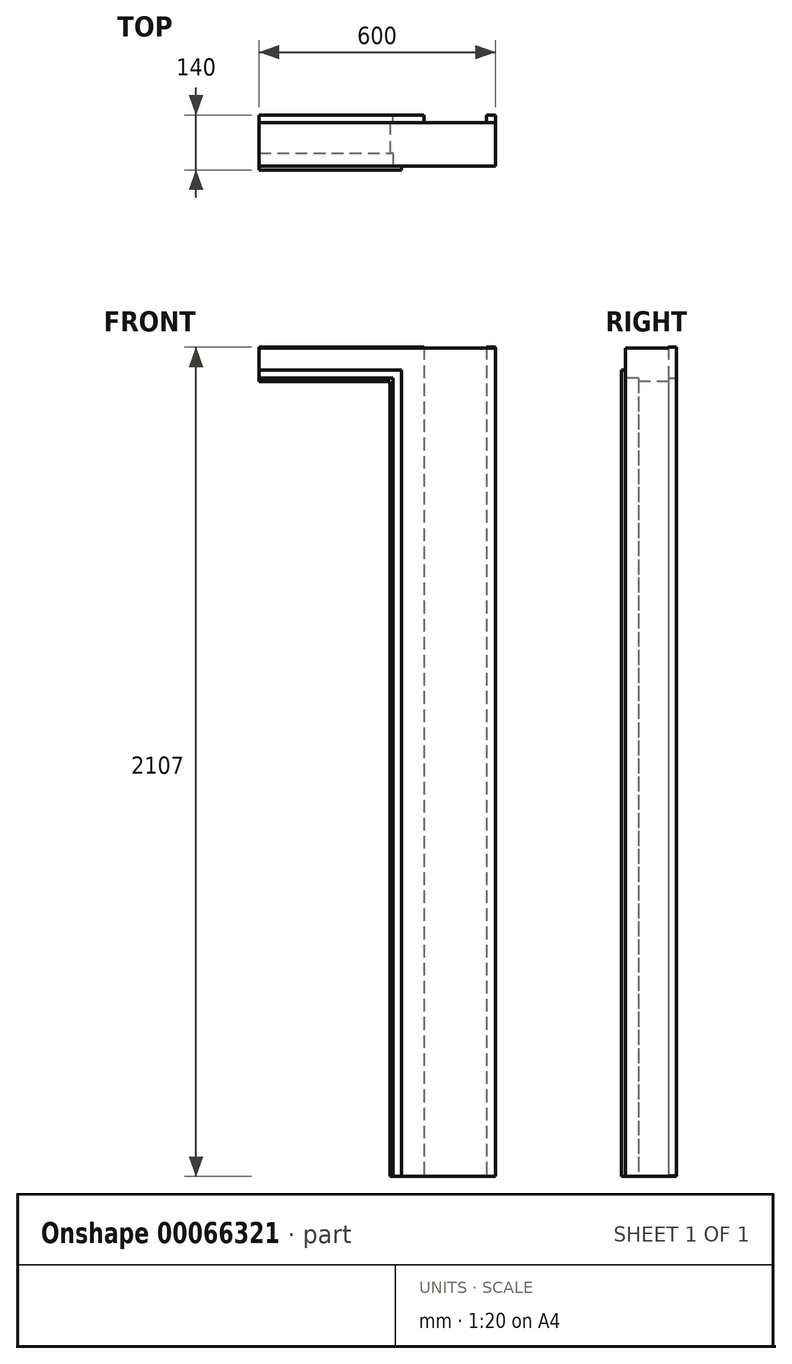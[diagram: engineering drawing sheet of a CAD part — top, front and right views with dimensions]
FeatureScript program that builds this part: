
annotation { "Feature Type Name" : "Feature", "Feature Type Description" : "" }
export const myFeature = defineFeature(function(context is Context, id is Id, definition is map)
    precondition{}
    {
        {
            var Q0;
            Q0=qCreatedBy(makeId("Front.planeOp"),FACE);
            var sketch = newSketch(context, id + "F0", { "sketchPlane" : qUnion([Q0])});
            skLineSegment(sketch, "E0.bottom", {"start": v(0, 0) * mm, "end": v(-600, 0) * mm});
            skLineSegment(sketch, "E0.top", {"start": v(0, -2105) * mm, "end": v(-260, -2105) * mm});
            skLineSegment(sketch, "E0.left", {"start": v(0, 0) * mm, "end": v(0, -2105) * mm});
            skLineSegment(sketch, "E0.right", {"start": v(-600, 0) * mm, "end": v(-600, -77) * mm});
            skLineSegment(sketch, "E1.top", {"start": v(-600, -77) * mm, "end": v(-260, -77) * mm});
            skLineSegment(sketch, "E1.right", {"start": v(-260, -2105) * mm, "end": v(-260, -77) * mm});
            skSolve(sketch);
        }
        {
            var Q0;
            Q0 = qSketchRegion(id + "F0", true);
            extrude(context, id + "F1", {"entities" : qUnion([Q0]), "oppositeDirection" : true, "depth" : (140 - 10 - 20) * mm});
        }
        {
            var Q0;
            Q0=makeQuery(id+"F1.opExtrude","CAP_FACE",FACE,{"disambiguationData":[OSD([sQuery(id+"F0.wireOp",EDGE,"E0.bottom"),sQuery(id+"F0.wireOp",EDGE,"E0.top"),sQuery(id+"F0.wireOp",EDGE,"E0.left"),sQuery(id+"F0.wireOp",EDGE,"E0.right"),sQuery(id+"F0.wireOp",EDGE,"E1.top"),sQuery(id+"F0.wireOp",EDGE,"E1.right")])],"isStart":true});
            var sketch = newSketch(context, id + "F2", { "sketchPlane" : qUnion([Q0])});
            skLineSegment(sketch, "E2", {"start": v(-600, -56) * mm, "end": v(-239, -56) * mm});
            skLineSegment(sketch, "E3", {"start": v(-239, -56) * mm, "end": v(-239, -2105) * mm});
            skLineSegment(sketch, "E4", {"start": v(-260, -77) * mm, "end": v(-239, -56) * mm, "construction": true});
            skSolve(sketch);
        }
        {
            var Q0;
            {var subQ3=sQuery(id+"F2.wireOp",EDGE,"E2");Q0=makeQuery(id+"F2.imprint","IMPRINT",FACE,{"disambiguationData":[TD([[makeQuery(id+"F2.imprint","IMPRINT",EDGE,{"derivedFrom":subQ3}),-1.0]])]});}
            extrude(context, id + "F3", {"entities" : qUnion([Q0]), "operationType" : NewBodyOperationType.ADD, "depth" : 10 * mm});
        }
        {
            var Q0;
            {var subQ0=sQuery(id+"F0.wireOp",EDGE,"E0.right");Q0=makeQuery(id+"F3.boolean.opBoolean","MERGE",FACE,{"derivedFrom":[makeQuery(id+"F1.opExtrude","SWEPT_FACE",FACE,{"disambiguationData":[OSD([subQ0])]}),makeQuery(id+"F3.opExtrude","SWEPT_FACE",FACE,{"disambiguationData":[OSD([subQ0])]})]});}
            var sketch = newSketch(context, id + "F4", { "sketchPlane" : qUnion([Q0])});
            skLineSegment(sketch, "E5.bottom", {"start": v(-110, -77) * mm, "end": v(-33, -77) * mm});
            skLineSegment(sketch, "E5.top", {"start": v(-110, -85) * mm, "end": v(-33, -85) * mm});
            skLineSegment(sketch, "E5.left", {"start": v(-110, -77) * mm, "end": v(-110, -85) * mm});
            skLineSegment(sketch, "E5.right", {"start": v(-33, -77) * mm, "end": v(-33, -85) * mm});
            skLineSegment(sketch, "E6.bottom", {"start": v(-110, -77) * mm, "end": v(-130, -77) * mm});
            skLineSegment(sketch, "E6.top", {"start": v(-110, 2) * mm, "end": v(-130, 2) * mm});
            skLineSegment(sketch, "E6.left", {"start": v(-110, -77) * mm, "end": v(-110, 2) * mm});
            skLineSegment(sketch, "E6.right", {"start": v(-130, -77) * mm, "end": v(-130, 2) * mm});
            skLineSegment(sketch, "E7.bottom", {"start": v(-110, -77) * mm, "end": v(-104.24, -77) * mm});
            skLineSegment(sketch, "E7.top", {"start": v(-110, -71.13) * mm, "end": v(-104.24, -71.13) * mm});
            skLineSegment(sketch, "E7.left", {"start": v(-110, -77) * mm, "end": v(-110, -71.13) * mm});
            skLineSegment(sketch, "E7.right", {"start": v(-104.24, -77) * mm, "end": v(-104.24, -71.13) * mm});
            skSolve(sketch);
        }
        {
            var Q0;
            Q0=makeQuery(id+"F4.imprint","IMPRINT",FACE,{"disambiguationData":[TD([[makeQuery(id+"F4.imprint","IMPRINT",EDGE,{"derivedFrom":sQuery(id+"F4.wireOp",EDGE,"E7.bottom")}),1.0]])]});
            var Q1;
            Q1=makeQuery(id+"F4.imprint","IMPRINT",FACE,{"disambiguationData":[TD([[makeQuery(id+"F4.imprint","IMPRINT",EDGE,{"derivedFrom":sQuery(id+"F4.wireOp",EDGE,"E5.bottom")}),-1.0]])]});
            var Q2;
            Q2=makeQuery(id+"F4.imprint","IMPRINT",FACE,{"disambiguationData":[TD([[makeQuery(id+"F4.imprint","IMPRINT",EDGE,{"derivedFrom":sQuery(id+"F4.wireOp",EDGE,"E6.bottom")}),-1.0]])]});
            var Q3;
            Q3=makeQuery(id+"F1.opExtrude","CAP_EDGE",EDGE,{"disambiguationData":[OSD([sQuery(id+"F0.wireOp",EDGE,"E1.top")])],"isStart":false});
            var Q4;
            Q4=makeQuery(id+"F1.opExtrude","CAP_EDGE",EDGE,{"disambiguationData":[OSD([sQuery(id+"F0.wireOp",EDGE,"E1.right")])],"isStart":false});
            sweep(context, id + "F5", {"operationType" : NewBodyOperationType.ADD, "profiles" : qUnion([Q0, Q1, Q2]), "path" : qUnion([Q3, Q4])});
        }
        {
            var Q0;
            Q0=makeQuery(id+"F5.opSweep","SWEPT_FACE",FACE,{"disambiguationData":[OSD([sQuery(id+"F0.wireOp",EDGE,"E1.top"),sQuery(id+"F4.wireOp",EDGE,"E6.top")])]});
            var sketch = newSketch(context, id + "F6", { "sketchPlane" : qUnion([Q0])});
            skLineSegment(sketch, "E8.bottom", {"start": v(0, 110) * mm, "end": v(-22, 110) * mm});
            skLineSegment(sketch, "E8.top", {"start": v(0, 130) * mm, "end": v(-22, 130) * mm});
            skLineSegment(sketch, "E8.left", {"start": v(0, 110) * mm, "end": v(0, 130) * mm});
            skLineSegment(sketch, "E8.right", {"start": v(-22, 110) * mm, "end": v(-22, 130) * mm});
            skSolve(sketch);
        }
        {
            var Q0;
            Q0=makeQuery(id+"F6.imprint","IMPRINT",FACE,{"disambiguationData":[TD([[makeQuery(id+"F6.imprint","IMPRINT",EDGE,{"derivedFrom":sQuery(id+"F6.wireOp",EDGE,"E8.bottom")}),-1.0]])]});
            var Q1;
            Q1=makeQuery(id+"F1.opExtrude","CAP_EDGE",EDGE,{"disambiguationData":[OSD([sQuery(id+"F0.wireOp",EDGE,"E0.left")])],"isStart":false});
            sweep(context, id + "F7", {"operationType" : NewBodyOperationType.ADD, "profiles" : qUnion([Q0]), "path" : qUnion([Q1])});
        }
    });
